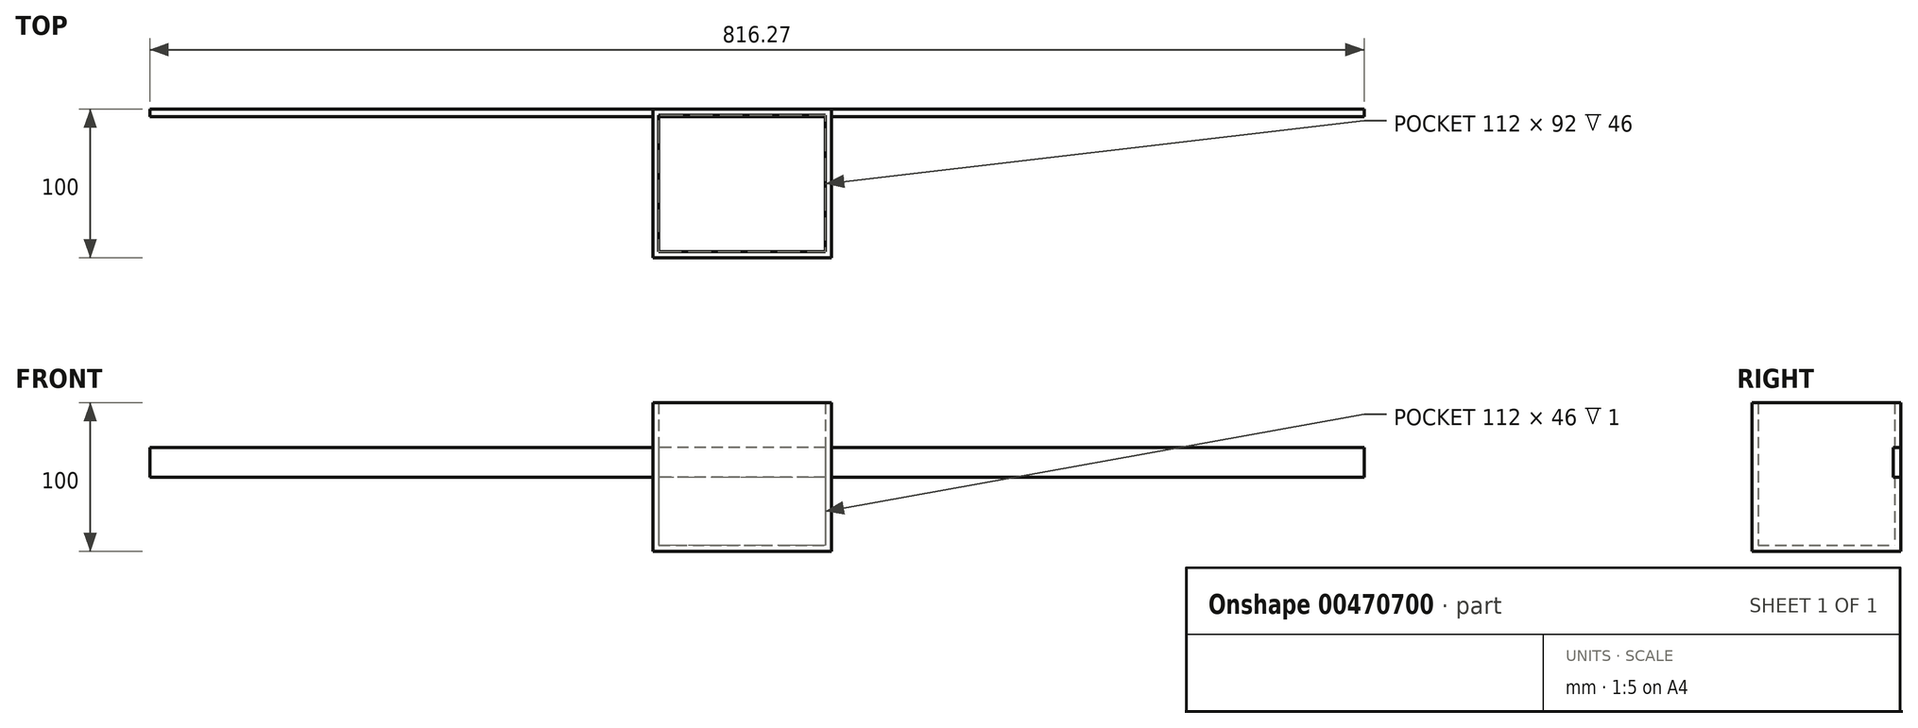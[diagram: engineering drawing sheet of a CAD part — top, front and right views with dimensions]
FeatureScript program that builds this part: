
annotation { "Feature Type Name" : "Feature", "Feature Type Description" : "" }
export const myFeature = defineFeature(function(context is Context, id is Id, definition is map)
    precondition{}
    {
        {
            var Q0;
            Q0=qCreatedBy(makeId("Top.planeOp"),FACE);
            var sketch = newSketch(context, id + "F0", { "sketchPlane" : qUnion([Q0])});
            skLineSegment(sketch, "E0.bottom", {"start": v(-94.06, -18.56) * mm, "end": v(25.94, -18.56) * mm});
            skLineSegment(sketch, "E0.top", {"start": v(-94.06, 81.44) * mm, "end": v(25.94, 81.44) * mm});
            skLineSegment(sketch, "E0.left", {"start": v(-94.06, -18.56) * mm, "end": v(-94.06, 81.44) * mm});
            skLineSegment(sketch, "E0.right", {"start": v(25.94, -18.56) * mm, "end": v(25.94, 81.44) * mm});
            skSolve(sketch);
        }
        {
            var Q0;
            Q0=makeQuery(id+"F0.imprint","IMPRINT",FACE,{"disambiguationData":[TD([[makeQuery(id+"F0.imprint","IMPRINT",EDGE,{"derivedFrom":sQuery(id+"F0.wireOp",EDGE,"E0.bottom")}),1.0]])]});
            extrude(context, id + "F1", {"entities" : qUnion([Q0]), "depth" : 100 * mm});
        }
        {
            var Q0;
            Q0=makeQuery(id+"F1.opExtrude","CAP_FACE",FACE,{"disambiguationData":[OSD([sQuery(id+"F0.wireOp",EDGE,"E0.bottom"),sQuery(id+"F0.wireOp",EDGE,"E0.top"),sQuery(id+"F0.wireOp",EDGE,"E0.left"),sQuery(id+"F0.wireOp",EDGE,"E0.right")])],"isStart":false});
            shell(context, id + "F2", {"entities" : qUnion([Q0]), "thickness" : 4 * mm});
        }
        {
            var Q0;
            Q0=makeQuery(id+"F1.opExtrude","SWEPT_FACE",FACE,{"disambiguationData":[OSD([sQuery(id+"F0.wireOp",EDGE,"E0.top")])]});
            var sketch = newSketch(context, id + "F3", { "sketchPlane" : qUnion([Q0])});
            skLineSegment(sketch, "E1.bottom", {"start": v(-384.07, 70) * mm, "end": v(432.2, 70) * mm});
            skLineSegment(sketch, "E1.top", {"start": v(-384.07, 50) * mm, "end": v(432.2, 50) * mm});
            skLineSegment(sketch, "E1.left", {"start": v(-384.07, 70) * mm, "end": v(-384.07, 50) * mm});
            skLineSegment(sketch, "E1.right", {"start": v(432.2, 70) * mm, "end": v(432.2, 50) * mm});
            skSolve(sketch);
        }
        {
            var Q0;
            {var subQ0=sQuery(id+"F3.wireOp",EDGE,"E1.right");Q0=makeQuery(id+"F3.imprint","IMPRINT",FACE,{"disambiguationData":[TD([[makeQuery(id+"F3.imprint","IMPRINT",EDGE,{"derivedFrom":subQ0}),-1.0]])]});}
            var Q1;
            {var subQ0=sQuery(id+"F3.wireOp",EDGE,"E1.bottom");var subQ1=sQuery(id+"F0.wireOp",EDGE,"E0.top");var subQ2=makeQuery(id+"F1.opExtrude","SWEPT_EDGE",EDGE,{"disambiguationData":[OSD([subQ1,sQuery(id+"F0.wireOp",EDGE,"E0.right")])]});var subQ3=makeQuery(id+"F3.imprint","INTERSECT",VERTEX,{"derivedFrom":[subQ2,subQ0]});Q1=makeQuery(id+"F3.imprint","IMPRINT",FACE,{"disambiguationData":[TD([[makeQuery(id+"F3.imprint","IMPRINT",EDGE,{"disambiguationData":[TD([[subQ3,-1.0]])],"derivedFrom":subQ0}),-1.0]])]});}
            var Q2;
            {var subQ0=sQuery(id+"F3.wireOp",EDGE,"E1.left");Q2=makeQuery(id+"F3.imprint","IMPRINT",FACE,{"disambiguationData":[TD([[makeQuery(id+"F3.imprint","IMPRINT",EDGE,{"derivedFrom":subQ0}),1.0]])]});}
            extrude(context, id + "F4", {"entities" : qUnion([Q0, Q1, Q2]), "operationType" : NewBodyOperationType.ADD, "oppositeDirection" : true, "depth" : 5 * mm});
        }
    });
